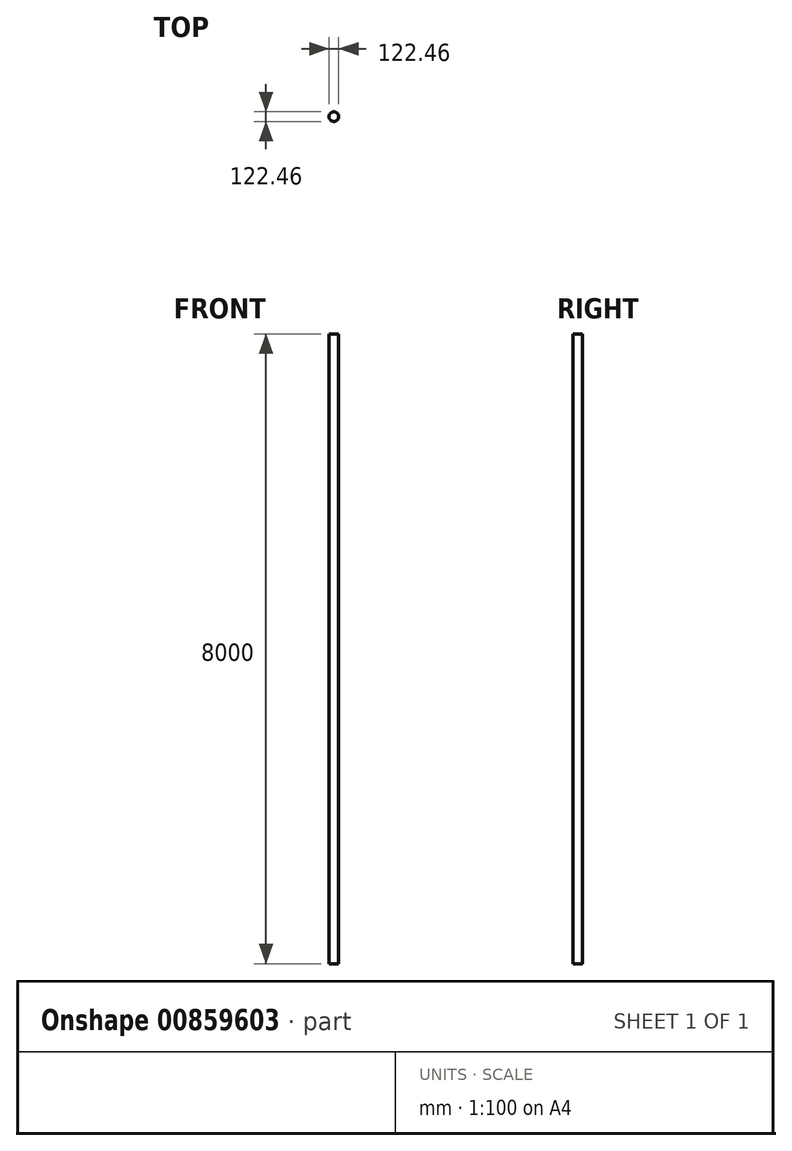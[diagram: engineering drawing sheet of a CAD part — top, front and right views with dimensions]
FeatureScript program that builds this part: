
annotation { "Feature Type Name" : "Feature", "Feature Type Description" : "" }
export const myFeature = defineFeature(function(context is Context, id is Id, definition is map)
    precondition{}
    {
        {
            var Q0;
            Q0=qCreatedBy(makeId("Top.planeOp"),FACE);
            var sketch = newSketch(context, id + "F0", { "sketchPlane" : qUnion([Q0])});
            skCircle(sketch, "E0", {"center": v(0, 0) * mm, "radius": 61.23 * mm});
            skSolve(sketch);
        }
        {
            var Q0;
            Q0 = qSketchRegion(id + "F0", true);
            extrude(context, id + "F1", {"entities" : qUnion([Q0]), "depth" : 8000 * mm, "offsetDistance" : 25 * mm});
        }
    });
